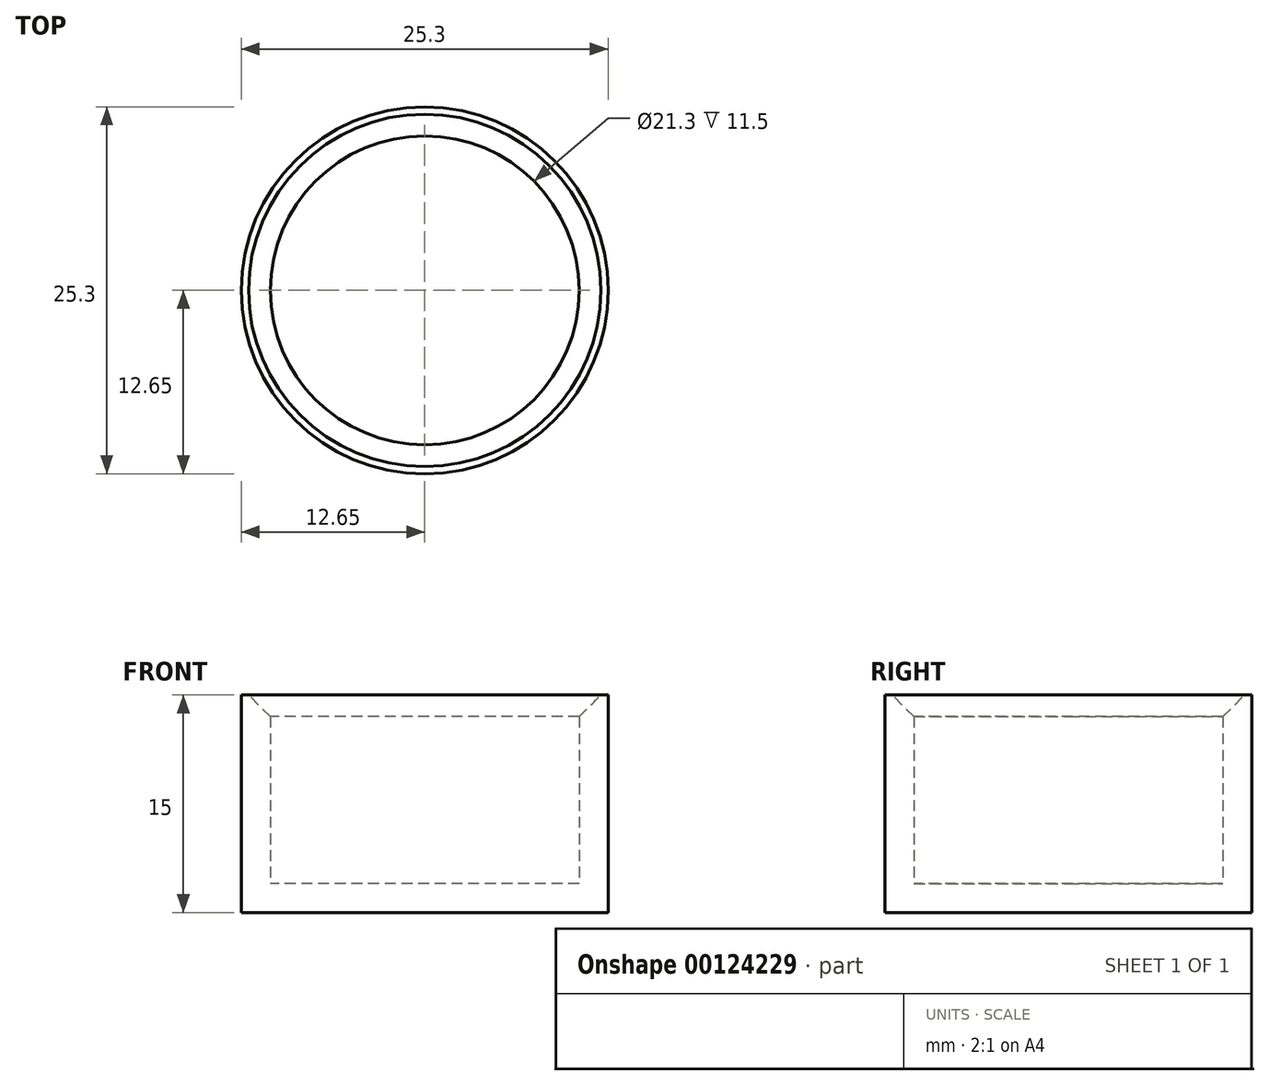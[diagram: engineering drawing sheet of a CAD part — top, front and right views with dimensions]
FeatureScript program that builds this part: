
annotation { "Feature Type Name" : "Feature", "Feature Type Description" : "" }
export const myFeature = defineFeature(function(context is Context, id is Id, definition is map)
    precondition{}
    {
        {
            var Q0;
            Q0=qCreatedBy(makeId("Top.planeOp"),FACE);
            var sketch = newSketch(context, id + "F0", { "sketchPlane" : qUnion([Q0])});
            skCircle(sketch, "E0", {"center": v(0, 0) * mm, "radius": 12.65 * mm});
            skSolve(sketch);
        }
        {
            var Q0;
            Q0=makeQuery(id+"F0.imprint","IMPRINT",FACE,{"disambiguationData":[TD([[makeQuery(id+"F0.imprint","IMPRINT",EDGE,{"derivedFrom":sQuery(id+"F0.wireOp",EDGE,"E0")}),1.0]])]});
            extrude(context, id + "F1", {"entities" : qUnion([Q0]), "depth" : 15 * mm});
        }
        {
            var Q0;
            Q0=makeQuery(id+"F1.opExtrude","CAP_FACE",FACE,{"disambiguationData":[OSD([sQuery(id+"F0.wireOp",EDGE,"E0")])],"isStart":false});
            shell(context, id + "F2", {"entities" : qUnion([Q0]), "thickness" : 2 * mm});
        }
        {
            var Q0;
            {var subQ0=sQuery(id+"F0.wireOp",EDGE,"E0");Q0=makeQuery(id+"F2.opShell","OFFSET_EDGE",EDGE,{"disambiguationData":[OSD([subQ0]),TDD([makeQuery(id+"F1.opExtrude","CAP_EDGE",EDGE,{"disambiguationData":[OSD([subQ0])],"isStart":false})])]});}
            chamfer(context, id + "F3", {"entities" : qUnion([Q0]), "width" : 1.5 * mm, "tangentPropagation" : true});
        }
    });
